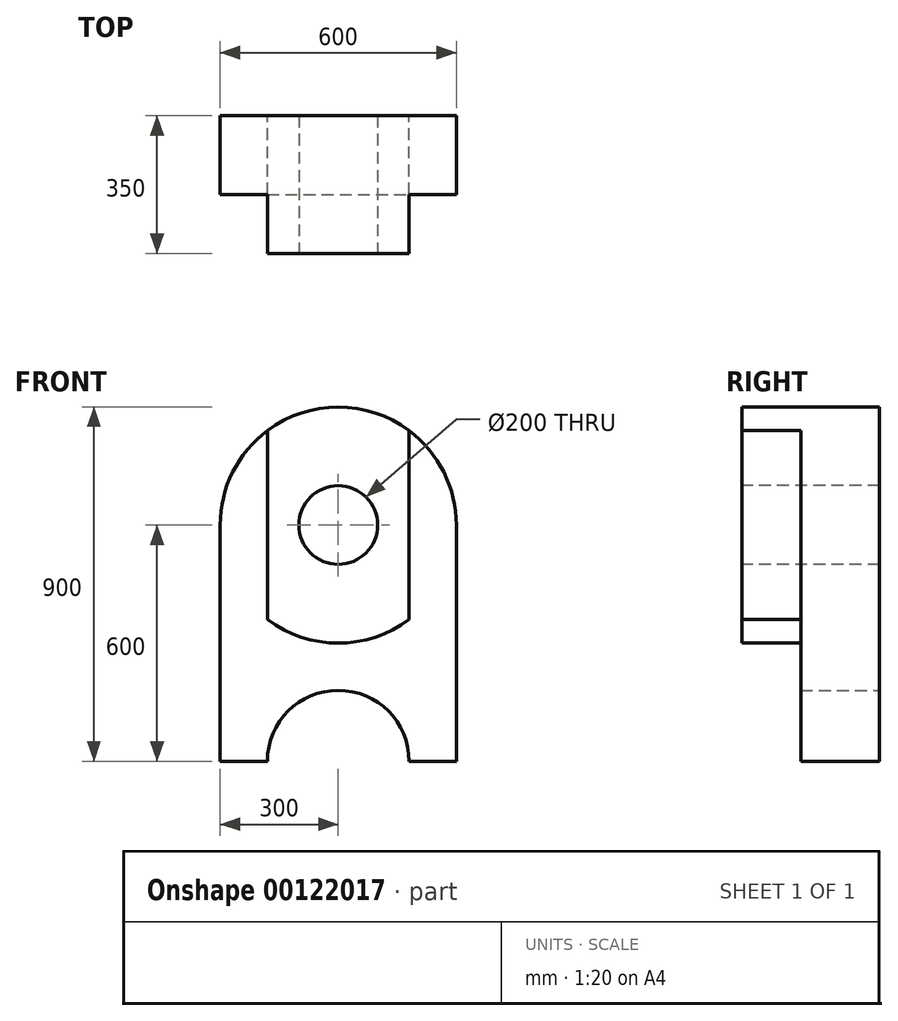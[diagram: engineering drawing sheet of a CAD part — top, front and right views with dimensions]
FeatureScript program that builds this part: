
annotation { "Feature Type Name" : "Feature", "Feature Type Description" : "" }
export const myFeature = defineFeature(function(context is Context, id is Id, definition is map)
    precondition{}
    {
        {
            var Q0;
            Q0=qCreatedBy(makeId("Front.planeOp"),FACE);
            var sketch = newSketch(context, id + "F0", { "sketchPlane" : qUnion([Q0])});
            skLineSegment(sketch, "E0.bottom", {"start": v(300, -300) * mm, "end": v(-300, -300) * mm});
            skLineSegment(sketch, "E0.top", {"start": v(300, 300) * mm, "end": v(-300, 300) * mm});
            skLineSegment(sketch, "E0.left", {"start": v(300, -300) * mm, "end": v(300, 300) * mm});
            skLineSegment(sketch, "E0.right", {"start": v(-300, -300) * mm, "end": v(-300, 300) * mm});
            skPoint(sketch, "E0.middle", {"position": v(0, 0) * mm});
            skArc(sketch, "E1", {"start": v(300, 300) * mm, "mid": v(0, 600) * mm, "end": v(-300, 300) * mm});
            skSolve(sketch);
        }
        {
            var Q0;
            Q0 = qSketchRegion(id + "F0", true);
            var Q1;
            Q1=makeQuery(id+"F0.imprint","IMPRINT",FACE,{"disambiguationData":[TD([[makeQuery(id+"F0.imprint","IMPRINT",EDGE,{"derivedFrom":sQuery(id+"F0.wireOp",EDGE,"E0.top")}),-1.0]])]});
            extrude(context, id + "F1", {"entities" : qUnion([Q0, Q1]), "depth" : 200 * mm});
        }
        {
            var Q0;
            Q0=makeQuery(id+"F1.opExtrude","CAP_FACE",FACE,{"disambiguationData":[OSD([sQuery(id+"F0.wireOp",EDGE,"E0.bottom"),sQuery(id+"F0.wireOp",EDGE,"E0.left"),sQuery(id+"F0.wireOp",EDGE,"E0.right"),sQuery(id+"F0.wireOp",EDGE,"E1")])],"isStart":true});
            var sketch = newSketch(context, id + "F2", { "sketchPlane" : qUnion([Q0])});
            skArc(sketch, "E2", {"start": v(180, -300) * mm, "mid": v(0, -120) * mm, "end": v(-180, -300) * mm});
            skSolve(sketch);
        }
        {
            var Q0;
            Q0 = qSketchRegion(id + "F2", true);
            var Q1;
            {var subQ0=sQuery(id+"F2.wireOp",EDGE,"E2");Q1=makeQuery(id+"F2.imprint","IMPRINT",FACE,{"disambiguationData":[TD([[makeQuery(id+"F2.imprint","IMPRINT",EDGE,{"derivedFrom":subQ0}),1.0]])]});}
            extrude(context, id + "F3", {"entities" : qUnion([Q0, Q1]), "operationType" : NewBodyOperationType.REMOVE, "endBound" : BoundingType.THROUGH_ALL, "oppositeDirection" : true, "depth" : 25 * mm});
        }
        {
            var Q0;
            Q0=makeQuery(id+"F1.opExtrude","CAP_FACE",FACE,{"disambiguationData":[OSD([sQuery(id+"F0.wireOp",EDGE,"E0.bottom"),sQuery(id+"F0.wireOp",EDGE,"E0.left"),sQuery(id+"F0.wireOp",EDGE,"E0.right"),sQuery(id+"F0.wireOp",EDGE,"E1")])],"isStart":false});
            var sketch = newSketch(context, id + "F4", { "sketchPlane" : qUnion([Q0])});
            skArc(sketch, "E3", {"start": v(180, 540) * mm, "mid": v(0, 600) * mm, "end": v(-180, 540) * mm});
            skLineSegment(sketch, "E4.left", {"start": v(180, 60) * mm, "end": v(180, 540) * mm});
            skLineSegment(sketch, "E4.right", {"start": v(-180, 60) * mm, "end": v(-180, 540) * mm});
            skArc(sketch, "E5.trimOffspring", {"start": v(-180, 60) * mm, "mid": v(0, 0) * mm, "end": v(180, 60) * mm});
            skPoint(sketch, "E4.bottom.end.orphan", {"position": v(-180, -258.49) * mm});
            skPoint(sketch, "E6.orphan", {"position": v(180, -258.49) * mm});
            skSolve(sketch);
        }
        {
            var Q0;
            Q0 = qSketchRegion(id + "F4", true);
            extrude(context, id + "F5", {"entities" : qUnion([Q0]), "operationType" : NewBodyOperationType.ADD, "depth" : 150 * mm});
        }
        {
            var Q0;
            Q0=makeQuery(id+"F5.opExtrude","CAP_FACE",FACE,{"disambiguationData":[OSD([sQuery(id+"F4.wireOp",EDGE,"E3"),sQuery(id+"F4.wireOp",EDGE,"E4.left"),sQuery(id+"F4.wireOp",EDGE,"E4.right"),sQuery(id+"F4.wireOp",EDGE,"E5.trimOffspring")])],"isStart":false});
            var sketch = newSketch(context, id + "F6", { "sketchPlane" : qUnion([Q0])});
            skCircle(sketch, "E7", {"center": v(0, 300) * mm, "radius": 100 * mm});
            skSolve(sketch);
        }
        {
            var Q0;
            Q0 = qSketchRegion(id + "F6", true);
            var Q1;
            Q1=makeQuery(id+"F6.imprint","IMPRINT",FACE,{"disambiguationData":[TD([[makeQuery(id+"F6.imprint","IMPRINT",EDGE,{"derivedFrom":sQuery(id+"F6.wireOp",EDGE,"E7")}),1.0]])]});
            extrude(context, id + "F7", {"entities" : qUnion([Q0, Q1]), "operationType" : NewBodyOperationType.REMOVE, "endBound" : BoundingType.THROUGH_ALL, "oppositeDirection" : true, "depth" : 25 * mm});
        }
    });
